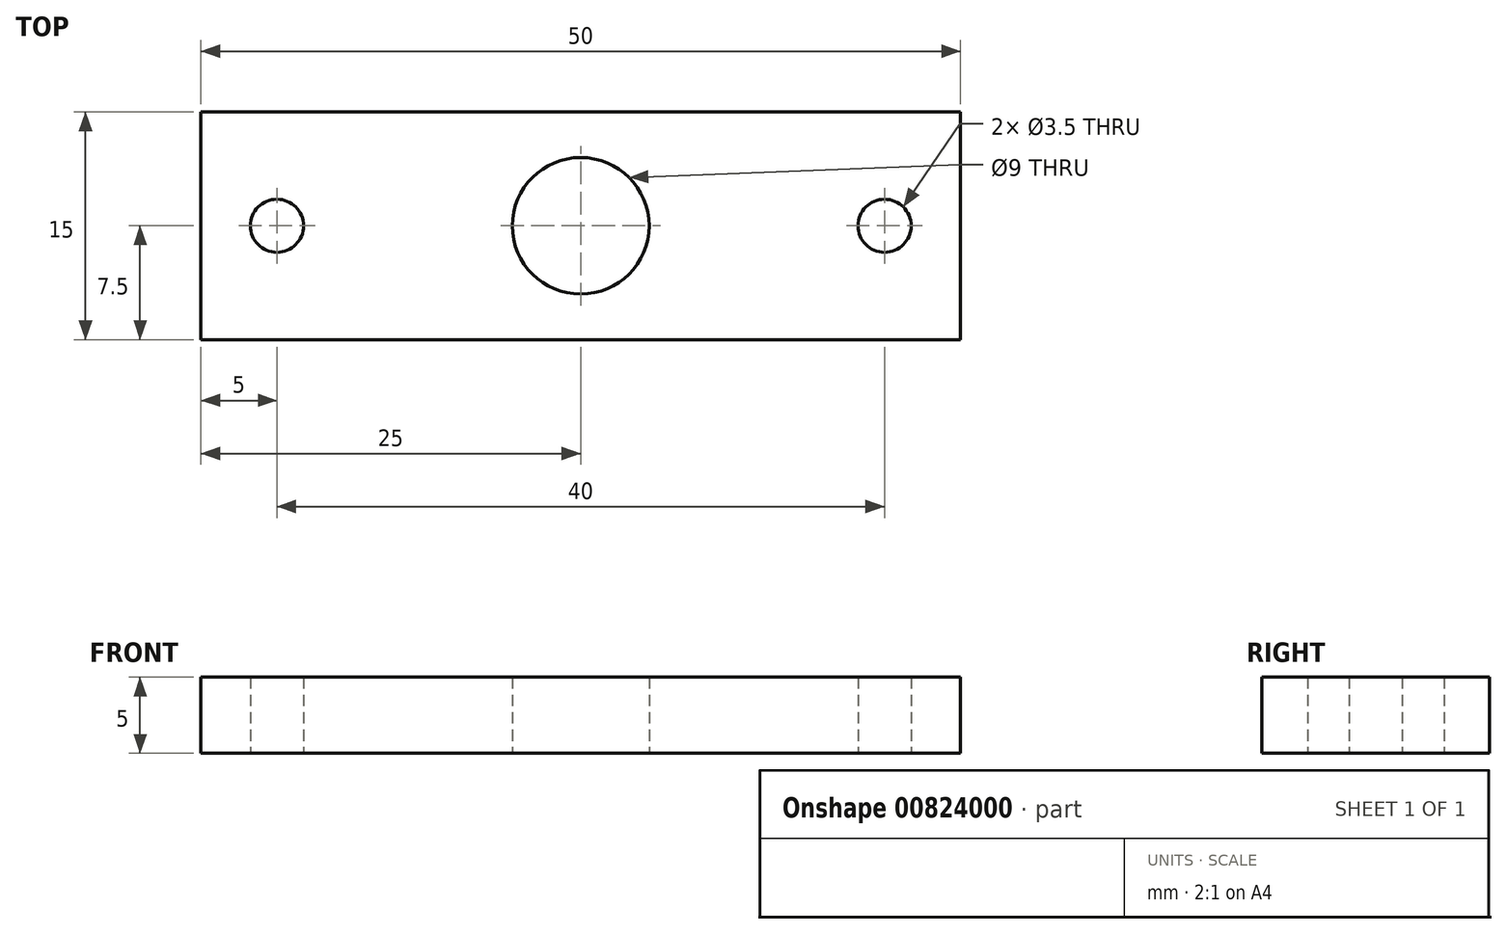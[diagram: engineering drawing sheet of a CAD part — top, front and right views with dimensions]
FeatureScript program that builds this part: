
annotation { "Feature Type Name" : "Feature", "Feature Type Description" : "" }
export const myFeature = defineFeature(function(context is Context, id is Id, definition is map)
    precondition{}
    {
        {
            var Q0;
            Q0=qCreatedBy(makeId("Top.planeOp"),FACE);
            var sketch = newSketch(context, id + "F0", { "sketchPlane" : qUnion([Q0])});
            skLineSegment(sketch, "E0.bottom", {"start": v(0, 0) * mm, "end": v(50, 0) * mm});
            skLineSegment(sketch, "E0.top", {"start": v(0, 15) * mm, "end": v(50, 15) * mm});
            skLineSegment(sketch, "E0.left", {"start": v(0, 0) * mm, "end": v(0, 15) * mm});
            skLineSegment(sketch, "E0.right", {"start": v(50, 0) * mm, "end": v(50, 15) * mm});
            skCircle(sketch, "E1", {"center": v(25, 7.5) * mm, "radius": 4.5 * mm});
            skPoint(sketch, "E1.centerSnap0", {"position": v(0, 7.5) * mm});
            skPoint(sketch, "E1.centerSnap1", {"position": v(25, 0) * mm});
            skCircle(sketch, "E2", {"center": v(5, 7.5) * mm, "radius": 1.75 * mm});
            skCircle(sketch, "E3", {"center": v(45, 7.5) * mm, "radius": 1.75 * mm});
            skPoint(sketch, "E3.centerSnap0", {"position": v(50, 7.5) * mm});
            skSolve(sketch);
        }
        {
            var Q0;
            Q0 = qSketchRegion(id + "F0", true);
            extrude(context, id + "F1", {"entities" : qUnion([Q0]), "depth" : 5 * mm, "offsetDistance" : 25 * mm});
        }
    });
